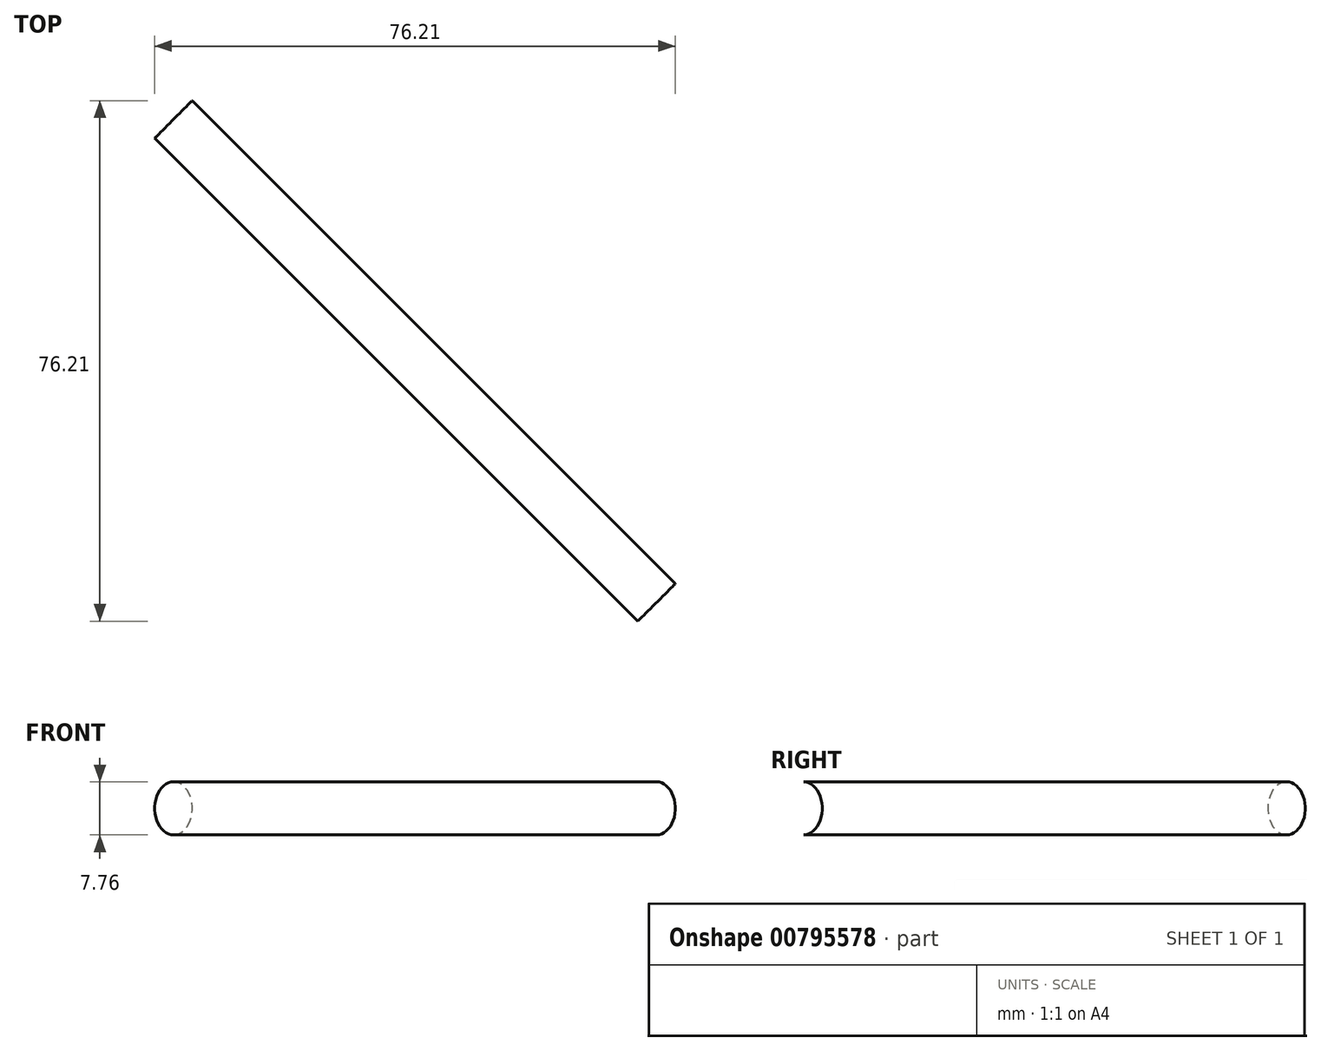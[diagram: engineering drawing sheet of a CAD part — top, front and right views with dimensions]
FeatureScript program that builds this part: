
annotation { "Feature Type Name" : "Feature", "Feature Type Description" : "" }
export const myFeature = defineFeature(function(context is Context, id is Id, definition is map)
    precondition{}
    {
        {
            var Q0;
            Q0=qCreatedBy(makeId("Front.planeOp"),FACE);
            var sketch = newSketch(context, id + "F0", { "sketchPlane" : qUnion([Q0])});
            skCircle(sketch, "E0", {"center": v(0, 0) * mm, "radius": 3.88 * mm});
            skLineSegment(sketch, "E1", {"start": v(0, 0) * mm, "end": v(0, 15.02) * mm, "construction": true});
            skSolve(sketch);
        }
        {
            var Q0;
            Q0=makeQuery(id+"F0.imprint","IMPRINT",FACE,{"disambiguationData":[TD([[makeQuery(id+"F0.imprint","IMPRINT",EDGE,{"derivedFrom":sQuery(id+"F0.wireOp",EDGE,"E0")}),1.0]])]});
            extrude(context, id + "F1", {"entities" : qUnion([Q0]), "depth" : 100 * mm, "offsetDistance" : 25 * mm});
        }
        {
            var Q0;
            Q0=makeQuery(id+"F1.opExtrude","SWEPT_BODY",BODY,{"disambiguationData":[OSD([sQuery(id+"F0.wireOp",EDGE,"E0")])]});
            var Q1;
            Q1=sQuery(id+"F0.wireOp",EDGE,"E1");
            transform(context, id + "F2", {"entities" : qUnion([Q0]), "transformType" : TransformType.ROTATION, "transformAxis" : qUnion([Q1]), "angle" : 45 * degree, "makeCopy" : false});
        }
    });
